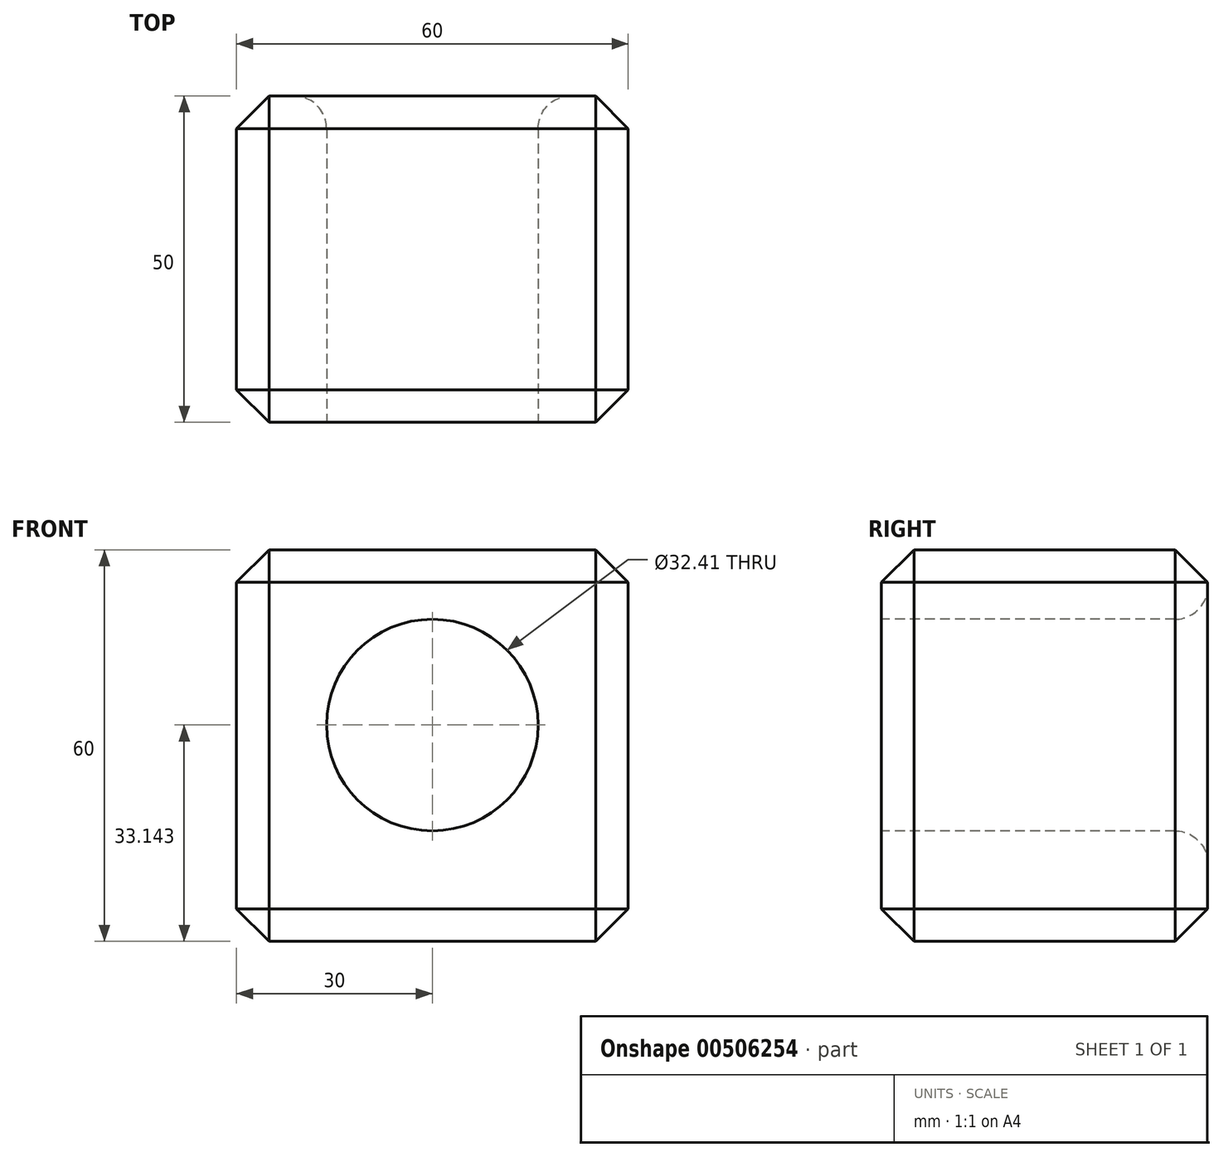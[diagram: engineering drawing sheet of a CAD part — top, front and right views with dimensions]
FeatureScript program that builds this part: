
annotation { "Feature Type Name" : "Feature", "Feature Type Description" : "" }
export const myFeature = defineFeature(function(context is Context, id is Id, definition is map)
    precondition{}
    {
        {
            var Q0;
            Q0=qCreatedBy(makeId("Top.planeOp"),FACE);
            var sketch = newSketch(context, id + "F0", { "sketchPlane" : qUnion([Q0])});
            skLineSegment(sketch, "E0.bottom", {"start": v(30, 25) * mm, "end": v(-30, 25) * mm});
            skLineSegment(sketch, "E0.top", {"start": v(30, -25) * mm, "end": v(-30, -25) * mm});
            skLineSegment(sketch, "E0.left", {"start": v(30, 25) * mm, "end": v(30, -25) * mm});
            skLineSegment(sketch, "E0.right", {"start": v(-30, 25) * mm, "end": v(-30, -25) * mm});
            skPoint(sketch, "E0.middle", {"position": v(0, 0) * mm});
            skSolve(sketch);
        }
        {
            var Q0;
            Q0=makeQuery(id+"F0.imprint","IMPRINT",FACE,{"disambiguationData":[TD([[makeQuery(id+"F0.imprint","IMPRINT",EDGE,{"derivedFrom":sQuery(id+"F0.wireOp",EDGE,"E0.bottom")}),1.0]])]});
            extrude(context, id + "F1", {"entities" : qUnion([Q0]), "depth" : 60 * mm});
        }
        {
            var Q0;
            Q0=makeQuery(id+"F1.opExtrude","SWEPT_FACE",FACE,{"disambiguationData":[OSD([sQuery(id+"F0.wireOp",EDGE,"E0.top")])]});
            var sketch = newSketch(context, id + "F2", { "sketchPlane" : qUnion([Q0])});
            skCircle(sketch, "E1", {"center": v(0, 33.14) * mm, "radius": 16.2 * mm});
            skSolve(sketch);
        }
        {
            var Q0;
            Q0=qSketchRegion(id+"F2",true);
            extrude(context, id + "F3", {"entities" : qUnion([Q0]), "operationType" : NewBodyOperationType.REMOVE, "endBound" : BoundingType.THROUGH_ALL, "oppositeDirection" : true, "depth" : 25 * mm});
        }
        {
            var Q0;
            Q0=makeQuery(id+"F3.boolean.opBoolean","COPY",EDGE,{"derivedFrom":makeQuery(id+"F3.opExtrude","CAP_EDGE",EDGE,{"disambiguationData":[OSD([sQuery(id+"F2.wireOp",EDGE,"E1")])],"isStart":true})});
            var Q1;
            Q1=makeQuery(id+"F3.boolean.opBoolean","INTERSECT",EDGE,{"derivedFrom":[makeQuery(id+"F1.opExtrude","SWEPT_FACE",FACE,{"disambiguationData":[OSD([sQuery(id+"F0.wireOp",EDGE,"E0.bottom")])]}),makeQuery(id+"F3.opExtrude","SWEPT_FACE",FACE,{"disambiguationData":[OSD([sQuery(id+"F2.wireOp",EDGE,"E1")])]})]});
            fillet(context, id + "F4", {"entities" : qUnion([Q0, Q1]), "radius" : 5 * mm, "tangentPropagation" : true, "allowEdgeOverflow" : false});
        }
        {
            var Q0;
            Q0=makeQuery(id+"F1.opExtrude","SWEPT_EDGE",EDGE,{"disambiguationData":[OSD([sQuery(id+"F0.wireOp",EDGE,"E0.bottom"),sQuery(id+"F0.wireOp",EDGE,"E0.right")])]});
            var Q1;
            Q1=makeQuery(id+"F1.opExtrude","SWEPT_EDGE",EDGE,{"disambiguationData":[OSD([sQuery(id+"F0.wireOp",EDGE,"E0.top"),sQuery(id+"F0.wireOp",EDGE,"E0.right")])]});
            var Q2;
            Q2=makeQuery(id+"F1.opExtrude","CAP_EDGE",EDGE,{"disambiguationData":[OSD([sQuery(id+"F0.wireOp",EDGE,"E0.right")])],"isStart":false});
            var Q3;
            Q3=makeQuery(id+"F1.opExtrude","CAP_EDGE",EDGE,{"disambiguationData":[OSD([sQuery(id+"F0.wireOp",EDGE,"E0.bottom")])],"isStart":false});
            var Q4;
            Q4=makeQuery(id+"F1.opExtrude","CAP_EDGE",EDGE,{"disambiguationData":[OSD([sQuery(id+"F0.wireOp",EDGE,"E0.top")])],"isStart":false});
            var Q5;
            Q5=makeQuery(id+"F1.opExtrude","CAP_EDGE",EDGE,{"disambiguationData":[OSD([sQuery(id+"F0.wireOp",EDGE,"E0.top")])],"isStart":true});
            var Q6;
            Q6=makeQuery(id+"F1.opExtrude","CAP_EDGE",EDGE,{"disambiguationData":[OSD([sQuery(id+"F0.wireOp",EDGE,"E0.right")])],"isStart":true});
            var Q7;
            Q7=makeQuery(id+"F1.opExtrude","SWEPT_EDGE",EDGE,{"disambiguationData":[OSD([sQuery(id+"F0.wireOp",EDGE,"E0.top"),sQuery(id+"F0.wireOp",EDGE,"E0.left")])]});
            var Q8;
            Q8=makeQuery(id+"F1.opExtrude","CAP_EDGE",EDGE,{"disambiguationData":[OSD([sQuery(id+"F0.wireOp",EDGE,"E0.left")])],"isStart":false});
            var Q9;
            Q9=makeQuery(id+"F1.opExtrude","SWEPT_EDGE",EDGE,{"disambiguationData":[OSD([sQuery(id+"F0.wireOp",EDGE,"E0.bottom"),sQuery(id+"F0.wireOp",EDGE,"E0.left")])]});
            var Q10;
            Q10=makeQuery(id+"F1.opExtrude","CAP_EDGE",EDGE,{"disambiguationData":[OSD([sQuery(id+"F0.wireOp",EDGE,"E0.left")])],"isStart":true});
            var Q11;
            Q11=makeQuery(id+"F1.opExtrude","CAP_EDGE",EDGE,{"disambiguationData":[OSD([sQuery(id+"F0.wireOp",EDGE,"E0.bottom")])],"isStart":true});
            chamfer(context, id + "F5", {"entities" : qUnion([Q0, Q1, Q2, Q3, Q4, Q5, Q6, Q7, Q8, Q9, Q10, Q11]), "width" : 5 * mm, "tangentPropagation" : true});
        }
    });
